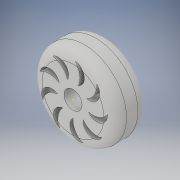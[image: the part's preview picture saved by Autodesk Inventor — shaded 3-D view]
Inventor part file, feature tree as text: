
AUTODESK INVENTOR PART (.ipt)
format: ipt  version: 2019 (Build 230136000, 136)  size: 250,880 bytes
history: native  units: mm
features: sketch x4, extrude x3, other x1, pattern_circular x1, fillet x1
ambient origin geometry x8: Origin, YZ Plane, XZ Plane, XY Plane, X Axis, Y Axis, Z Axis, Center Point
bodies: Body1 (feature_tree), Body2 (feature_tree), Body3 (feature_tree)
feature tree (10):
  other  "Bryła1"
  extrude  "Wyciągnięcie proste1"  Depth=14.9mm
  extrude  "Wyciągnięcie proste2"  Depth=6.0mm TaperAngle=0.0deg
  sketch  "Szkic3"
  extrude  "Wyciągnięcie proste3"  Depth=3.2mm
  pattern_circular  "Szyk kołowy1"  [2 undecoded]
  fillet  "Zaokrąglenie1"  Radius=3.45mm
  sketch  "Szkic1"
  sketch  "Szkic2"
  sketch  "Szkic4"
note: 2 required parameter values undecoded (feature->parameter linkage not recoverable at this tier; creation-order binding heuristic only, values carry confidence <= 0.55)
